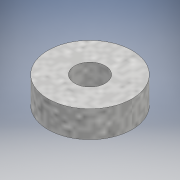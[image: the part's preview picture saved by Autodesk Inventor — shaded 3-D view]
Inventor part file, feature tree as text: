
AUTODESK INVENTOR PART (.ipt)
format: ipt  version: 2017 (Build 210142000, 142)  size: 106,496 bytes
history: native  units: mm
features: extrude x1, sketch x1
ambient origin geometry x8: Origin, YZ Plane, XZ Plane, XY Plane, X Axis, Y Axis, Z Axis, Center Point
bodies: Solid1 (feature_tree)
feature tree (2):
  extrude  "Extrusion1"  Depth=7.0mm
  sketch  "Sketch1"  dims[d0=8.0mm d1=22.0mm d2=7.0mm d3=0.0mm]
